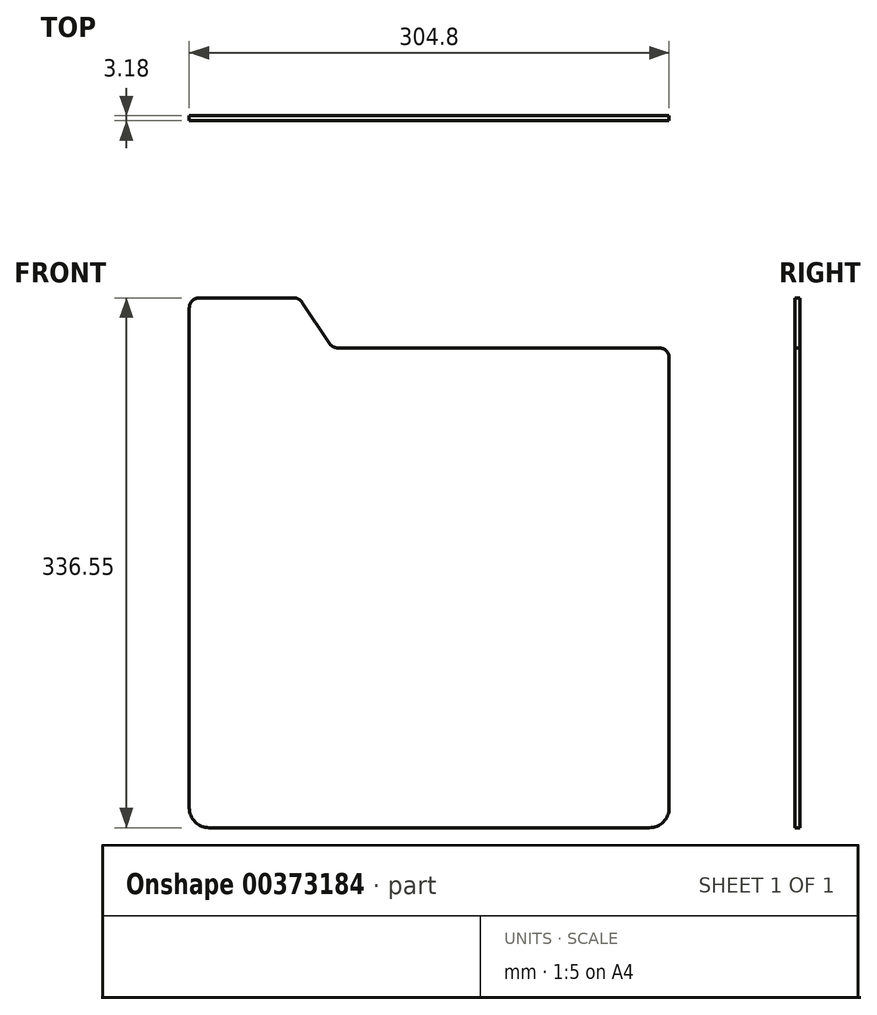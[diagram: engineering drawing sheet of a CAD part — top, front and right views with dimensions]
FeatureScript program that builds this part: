
annotation { "Feature Type Name" : "Feature", "Feature Type Description" : "" }
export const myFeature = defineFeature(function(context is Context, id is Id, definition is map)
    precondition{}
    {
        {
            var Q0;
            Q0=qCreatedBy(makeId("Front.planeOp"),FACE);
            var sketch = newSketch(context, id + "F0", { "sketchPlane" : qUnion([Q0])});
            skLineSegment(sketch, "E0.top", {"start": v(-152.4, -152.4) * mm, "end": v(152.4, -152.4) * mm});
            skLineSegment(sketch, "E0.left", {"start": v(-152.4, 152.4) * mm, "end": v(-152.4, -152.4) * mm});
            skLineSegment(sketch, "E0.right", {"start": v(152.4, 152.4) * mm, "end": v(152.4, -152.4) * mm});
            skPoint(sketch, "E0.middle", {"position": v(0, 0) * mm});
            skLineSegment(sketch, "E1.top", {"start": v(-152.4, 184.15) * mm, "end": v(-82.55, 184.15) * mm});
            skLineSegment(sketch, "E1.left", {"start": v(-152.4, 152.4) * mm, "end": v(-152.4, 184.15) * mm});
            skLineSegment(sketch, "E2.trimOffspring", {"start": v(-61.47, 152.4) * mm, "end": v(152.4, 152.4) * mm});
            skLineSegment(sketch, "E3", {"start": v(-82.55, 184.15) * mm, "end": v(-61.47, 152.4) * mm});
            skSolve(sketch);
        }
        {
            var Q0;
            Q0=makeQuery(id+"F0.imprint","IMPRINT",FACE,{"disambiguationData":[TD([[makeQuery(id+"F0.imprint","IMPRINT",EDGE,{"derivedFrom":sQuery(id+"F0.wireOp",EDGE,"E0.top")}),1.0]])]});
            extrude(context, id + "F1", {"entities" : qUnion([Q0]), "endBound" : BoundingType.SYMMETRIC, "depth" : 3.17 * mm});
        }
        {
            var Q0;
            Q0=makeQuery(id+"F1.opExtrude","SWEPT_EDGE",EDGE,{"disambiguationData":[OSD([sQuery(id+"F0.wireOp",EDGE,"E0.right"),sQuery(id+"F0.wireOp",EDGE,"E2.trimOffspring")])]});
            var Q1;
            Q1=makeQuery(id+"F1.opExtrude","SWEPT_EDGE",EDGE,{"disambiguationData":[OSD([sQuery(id+"F0.wireOp",EDGE,"sXBlhq2e-Az9E-PsWb-R7RK-MqVsCuO4aR0d"),sQuery(id+"F0.wireOp",EDGE,"E2.trimOffspring")])]});
            var Q2;
            Q2=makeQuery(id+"F1.opExtrude","SWEPT_EDGE",EDGE,{"disambiguationData":[OSD([sQuery(id+"F0.wireOp",EDGE,"E1.top"),sQuery(id+"F0.wireOp",EDGE,"sXBlhq2e-Az9E-PsWb-R7RK-MqVsCuO4aR0d")])]});
            var Q3;
            Q3=makeQuery(id+"F1.opExtrude","SWEPT_EDGE",EDGE,{"disambiguationData":[OSD([sQuery(id+"F0.wireOp",EDGE,"E1.top"),sQuery(id+"F0.wireOp",EDGE,"E1.left")])]});
            fillet(context, id + "F2", {"entities" : qUnion([Q0, Q1, Q2, Q3]), "radius" : 6.35 * mm, "tangentPropagation" : true, "allowEdgeOverflow" : false});
        }
        {
            var Q0;
            Q0=makeQuery(id+"F1.opExtrude","SWEPT_EDGE",EDGE,{"disambiguationData":[OSD([sQuery(id+"F0.wireOp",EDGE,"E0.top"),sQuery(id+"F0.wireOp",EDGE,"E0.right")])]});
            var Q1;
            Q1=makeQuery(id+"F1.opExtrude","SWEPT_EDGE",EDGE,{"disambiguationData":[OSD([sQuery(id+"F0.wireOp",EDGE,"E0.top"),sQuery(id+"F0.wireOp",EDGE,"E0.left")])]});
            fillet(context, id + "F3", {"entities" : qUnion([Q0, Q1]), "radius" : 12.7 * mm, "tangentPropagation" : true, "allowEdgeOverflow" : false});
        }
    });
